# Revit family: Golf-IP40-Plain_Door-syst-IT-en
name_source: partatom
category: Electrical Equipment
units: mm (PartAtom-declared; Revit-internal decimal feet)

## family parameters
Cut with Voids When Loaded = No
Host = Face
Panel Configuration = Two Columns, Circuits Across
Part Type = Panelboard
Room Calculation Point = No
Round Connector Dimension = Use Diameter
Shared = No

## types (22) — shared parameters
EF000007 - Colour = EV000202 - White
EF000049 - Depth = 98 mm  [stored 0.321522 ft]
EF000116 - RAL-number = 9010
EF000118 - With mounting plate = No
EF000339 - Type of cover = EV004216 - Door
EF001062 - EMC-version = No
EF001088 - Extension possible = Yes
EF001131 - Internal depth = 98 mm  [stored 0.321522 ft]
EF001134 - DIN-rail = Yes
EF001596 - Material housing = EV000139 - Plastic
EF004462 - Type of closure = EV000154 - Other
EF005474 - Degree of protection (IP) = EV006415 - IP40
EF006244 - Transparent cover/door = No
EF006306 - With lock = No
EF009212 - Cover model = EV000116 - Closed
EF015776 - Earthing terminal block = No
EF015777 - Neutral terminal block = No
EF015941 - Signal passing door = No
HG000001 - Number of columns = 1
HG000002 - With door or cover = Yes
HG000003 - Range = Golf
HG000005 - Thickness = 3 mm  [stored 0.00984252 ft]
HG000009 - Double swing door = No
HG000010 - Asymmetric doors = No
HG000011 - Empty rows from bottom = No
Manufacturer = Hager
Type Comments = Golf
zero-valued in all types: Default Elevation, HG000007 - Number of empty columns, HG000008 - Number of empty rows

## per-type parameters (varying)
| type | EF000003 - Mounting method | EF000008 - Width | EF000040 - Height | EF000218 - Built-in depth | EF000266 - Number of rows | EF000332 - Built-in height | EF000846 - Built-in width | EF002950 - Width in number of modular spacings | HG000004 - Manufacturer reference | HG000006 - Flush mounted | Model |
| Recessed mounted IP40 W204 H225 D97.5 4 Modular spacings - VF104PG | EV000383 - Flush mounted (plaster) | 204 mm | 225 mm | 72 mm  [stored 0.23622 ft] | 1 | 189 mm | 170 mm | 4 | VF104PG | Yes | VF104PG |
| Recessed mounted IP40 W275 H225 D97.5 8 Modular spacings - VF108PG | EV000383 - Flush mounted (plaster) | 275 mm | 225 mm | 72 mm  [stored 0.23622 ft] | 1 | 189 mm | 242 mm | 8 | VF108PG | Yes | VF108PG |
| Recessed mounted IP40 W352 H293 D97.5 12 Modular spacings - VF112PG | EV000383 - Flush mounted (plaster) | 352 mm | 293 mm | 72 mm  [stored 0.23622 ft] | 1 | 257 mm | 318 mm | 12 | VF112PG | Yes | VF112PG |
| Recessed mounted IP40 W352 H418 D97.5 12 Modular spacings - VF212PG | EV000383 - Flush mounted (plaster) | 352 mm | 418 mm | 72 mm  [stored 0.23622 ft] | 2 | 382 mm | 318 mm | 12 | VF212PG | Yes | VF212PG |
| Recessed mounted IP40 W352 H543 D97.5 12 Modular spacings - VF312PG | EV000383 - Flush mounted (plaster) | 352 mm | 543 mm | 72 mm  [stored 0.23622 ft] | 3 | 507 mm | 318 mm | 12 | VF312PG | Yes | VF312PG |
| Recessed mounted IP40 W352 H688 D97.5 12 Modular spacings - VF412PG | EV000383 - Flush mounted (plaster) | 352 mm | 688 mm | 72 mm  [stored 0.23622 ft] | 4 | 652 mm | 318 mm | 12 | VF412PG | Yes | VF412PG |
| Recessed mounted IP40 W460 H293 D97.5 18 Modular spacings - VF118PG | EV000383 - Flush mounted (plaster) | 460 mm | 293 mm | 72 mm  [stored 0.23622 ft] | 1 | 257 mm | 426 mm | 18 | VF118PG | Yes | VF118PG |
| Recessed mounted IP40 W460 H418 D97.5 18 Modular spacings - VF218PG | EV000383 - Flush mounted (plaster) | 460 mm | 418 mm | 72 mm  [stored 0.23622 ft] | 2 | 382 mm | 426 mm | 18 | VF218PG | Yes | VF218PG |
| Recessed mounted IP40 W460 H543 D97.5 18 Modular spacings - VF318PG | EV000383 - Flush mounted (plaster) | 460 mm | 543 mm | 72 mm  [stored 0.23622 ft] | 3 | 507 mm | 426 mm | 18 | VF318PG | Yes | VF318PG |
| Recessed mounted IP40 W460 H688 D97.5 18 Modular spacings - VF418PG | EV000383 - Flush mounted (plaster) | 460 mm | 688 mm | 72 mm  [stored 0.23622 ft] | 4 | 652 mm | 426 mm | 18 | VF418PG | Yes | VF418PG |
| Recessed mounted IP40 W532 H293 D97.5 22 Modular spacings - VF122PG | EV000383 - Flush mounted (plaster) | 532 mm | 293 mm | 72 mm  [stored 0.23622 ft] | 1 | 257 mm | 498 mm  [stored 1.63386 ft] | 22 | VF122PG | Yes | VF122PG |
| Surface mounted IP40 W137.5 H183.5 D98.5 4 Modular spacings - VS104PG | EV000384 - Surface mounted (plaster) | 138 mm | 184 mm | 0 mm  [stored 0 ft] | 1 | 0 mm  [stored 0 ft] | 0 mm  [stored 0 ft] | 4 | VS104PG | No | VS104PG |
| Surface mounted IP40 W209.5 H183.5 D98.5 8 Modular spacings - VS108PG | EV000384 - Surface mounted (plaster) | 210 mm | 184 mm | 0 mm  [stored 0 ft] | 1 | 0 mm  [stored 0 ft] | 0 mm  [stored 0 ft] | 8 | VS108PG | No | VS108PG |
| Surface mounted IP40 W281.5 H251.5 D98.5 12 Modular spacings - VS112PG | EV000384 - Surface mounted (plaster) | 282 mm | 252 mm  [stored 0.826772 ft] | 0 mm  [stored 0 ft] | 1 | 0 mm  [stored 0 ft] | 0 mm  [stored 0 ft] | 12 | VS112PG | No | VS112PG |
| Surface mounted IP40 W281.5 H376.5 D98.5 12 Modular spacings - VS212PG | EV000384 - Surface mounted (plaster) | 282 mm | 376 mm | 0 mm  [stored 0 ft] | 2 | 0 mm  [stored 0 ft] | 0 mm  [stored 0 ft] | 12 | VS212PG | No | VS212PG |
| Surface mounted IP40 W281.5 H501.5 D98.5 12 Modular spacings - VS312PG | EV000384 - Surface mounted (plaster) | 282 mm | 502 mm | 0 mm  [stored 0 ft] | 3 | 0 mm  [stored 0 ft] | 0 mm  [stored 0 ft] | 12 | VS312PG | No | VS312PG |
| Surface mounted IP40 W281.5 H646.5 D98.5 12 Modular spacings - VS412PG | EV000384 - Surface mounted (plaster) | 282 mm | 646 mm | 0 mm  [stored 0 ft] | 4 | 0 mm  [stored 0 ft] | 0 mm  [stored 0 ft] | 12 | VS412PG | No | VS412PG |
| Surface mounted IP40 W389.5 H251.5 D98.5 18 Modular spacings - VS118PG | EV000384 - Surface mounted (plaster) | 390 mm | 252 mm  [stored 0.826772 ft] | 0 mm  [stored 0 ft] | 1 | 0 mm  [stored 0 ft] | 0 mm  [stored 0 ft] | 18 | VS118PG | No | VS118PG |
| Surface mounted IP40 W389.5 H376.5 D98.5 18 Modular spacings - VS218PG | EV000384 - Surface mounted (plaster) | 390 mm | 376 mm | 0 mm  [stored 0 ft] | 2 | 0 mm  [stored 0 ft] | 0 mm  [stored 0 ft] | 18 | VS218PG | No | VS218PG |
| Surface mounted IP40 W389.5 H501.5 D98.5 18 Modular spacings - VS318PG | EV000384 - Surface mounted (plaster) | 390 mm | 502 mm | 0 mm  [stored 0 ft] | 3 | 0 mm  [stored 0 ft] | 0 mm  [stored 0 ft] | 18 | VS318PG | No | VS318PG |
| Surface mounted IP40 W389.5 H646.5 D98.5 18 Modular spacings - VS418PG | EV000384 - Surface mounted (plaster) | 390 mm | 646 mm | 0 mm  [stored 0 ft] | 4 | 0 mm  [stored 0 ft] | 0 mm  [stored 0 ft] | 18 | VS418PG | No | VS418PG |
| Surface mounted IP40 W461.5 H251.5 D98.5 22 Modular spacings - VS122PG | EV000384 - Surface mounted (plaster) | 462 mm  [stored 1.51575 ft] | 252 mm  [stored 0.826772 ft] | 0 mm  [stored 0 ft] | 1 | 0 mm  [stored 0 ft] | 0 mm  [stored 0 ft] | 22 | VS122PG | No | VS122PG |

note: [stored X ft] marks values corroborated as IEEE doubles in the binary element streams (Revit-internal decimal feet)

## geometry (parser evidence)
native form markers: Sweep x11
no freeform markers — native parametric forms only
